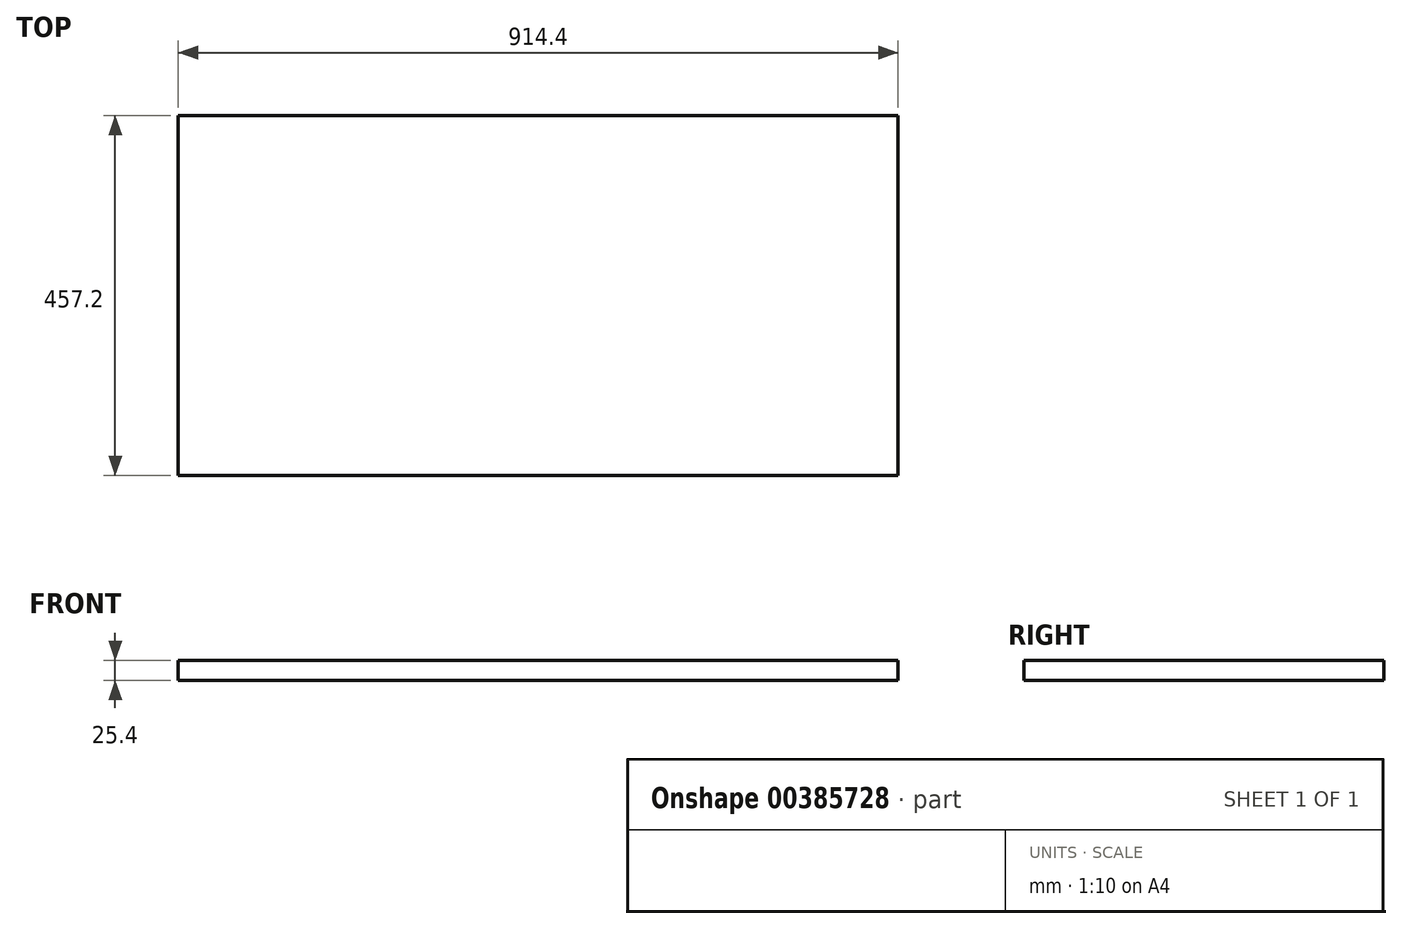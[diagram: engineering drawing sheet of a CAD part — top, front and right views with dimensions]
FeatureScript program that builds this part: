
annotation { "Feature Type Name" : "Feature", "Feature Type Description" : "" }
export const myFeature = defineFeature(function(context is Context, id is Id, definition is map)
    precondition{}
    {
        {
            var Q0;
            Q0=qCreatedBy(makeId("Top.planeOp"),FACE);
            var sketch = newSketch(context, id + "F0", { "sketchPlane" : qUnion([Q0])});
            skLineSegment(sketch, "E0.bottom", {"start": v(457.2, -228.6) * mm, "end": v(-457.2, -228.6) * mm});
            skLineSegment(sketch, "E0.top", {"start": v(457.2, 228.6) * mm, "end": v(-457.2, 228.6) * mm});
            skLineSegment(sketch, "E0.left", {"start": v(457.2, -228.6) * mm, "end": v(457.2, 228.6) * mm});
            skLineSegment(sketch, "E0.right", {"start": v(-457.2, -228.6) * mm, "end": v(-457.2, 228.6) * mm});
            skPoint(sketch, "E0.middle", {"position": v(0, 0) * mm});
            skSolve(sketch);
        }
        {
            var Q0;
            Q0=makeQuery(id+"F0.imprint","IMPRINT",FACE,{"disambiguationData":[TD([[makeQuery(id+"F0.imprint","IMPRINT",EDGE,{"derivedFrom":sQuery(id+"F0.wireOp",EDGE,"E0.bottom")}),-1.0]])]});
            extrude(context, id + "F1", {"entities" : qUnion([Q0]), "depth" : 25.4 * mm});
        }
    });
